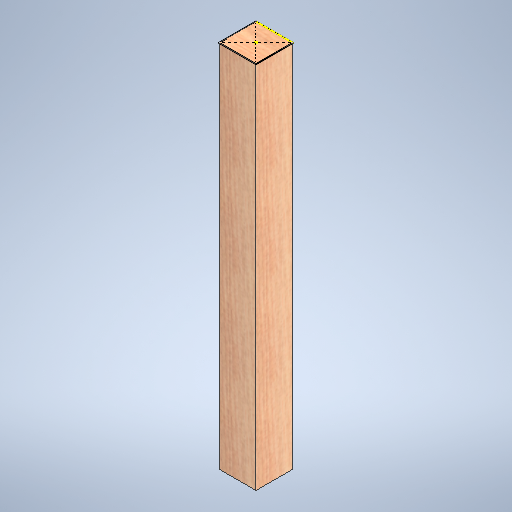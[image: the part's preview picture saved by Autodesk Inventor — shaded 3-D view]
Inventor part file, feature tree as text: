
AUTODESK INVENTOR PART (.ipt)
format: ipt  version: 2025 (Build 290162000, 162)  size: 339,456 bytes
history: native  units: in
note: dims shown in document units (in); Inventor stores cm internally (conversion verified against a paired STEP export)
features: sketch x2, extrude x1
ambient origin geometry x8: Origin, YZ Plane, XZ Plane, XY Plane, X Axis, Y Axis, Z Axis, Center Point
bodies: Solid1 (feature_tree)
feature tree (3):
  extrude  "Extrusion1"  Depth=4.0in
  sketch  "Sketch2"  dims[d2=40.0in d3=0.0in d4=0.5in d5=0.0344in d6=0.5in d7=0.0344in]
  sketch  "Sketch1"  dims[d0=4.0in d1=4.0in]
